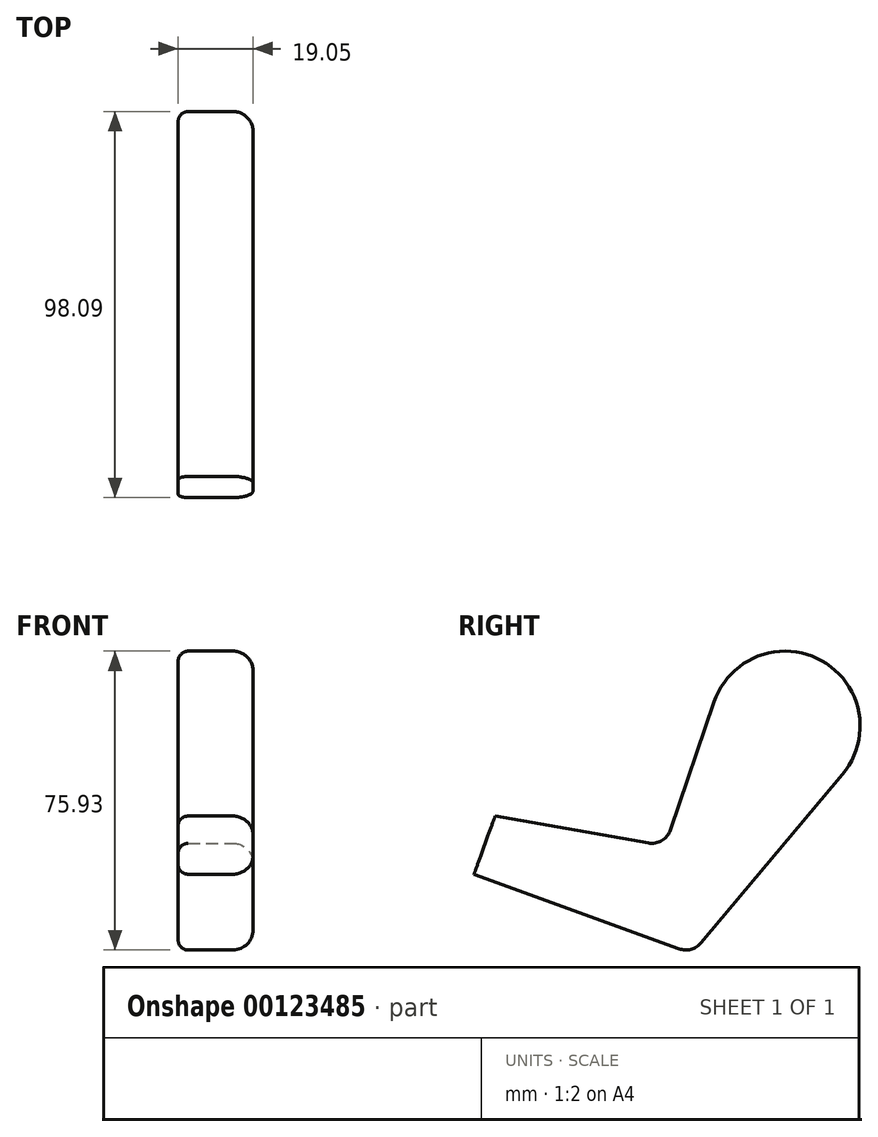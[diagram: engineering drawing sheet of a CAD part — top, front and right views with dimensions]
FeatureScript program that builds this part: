
annotation { "Feature Type Name" : "Feature", "Feature Type Description" : "" }
export const myFeature = defineFeature(function(context is Context, id is Id, definition is map)
    precondition{}
    {
        {
            var Q0;
            Q0=qCreatedBy(makeId("Front.planeOp"),FACE);
            var sketch = newSketch(context, id + "F0", { "sketchPlane" : qUnion([Q0])});
            skLineSegment(sketch, "E0", {"start": v(-26.99, 0) * mm, "end": v(26.99, 0) * mm});
            skLineSegment(sketch, "E1", {"start": v(26.99, 0) * mm, "end": v(38.1, 57.15) * mm});
            skLineSegment(sketch, "E2", {"start": v(38.1, 57.15) * mm, "end": v(38.1, 101.6) * mm});
            skLineSegment(sketch, "E3", {"start": v(38.1, 101.6) * mm, "end": v(-38.1, 101.6) * mm});
            skLineSegment(sketch, "E4", {"start": v(-38.1, 101.6) * mm, "end": v(-38.1, 57.15) * mm});
            skLineSegment(sketch, "E5", {"start": v(-38.1, 57.15) * mm, "end": v(-26.99, 0) * mm});
            skLineSegment(sketch, "E6", {"start": v(0, 0) * mm, "end": v(0, 101.6) * mm, "construction": true});
            skSolve(sketch);
        }
        {
            var Q0;
            Q0=qSketchRegion(id+"F0",true);
            extrude(context, id + "F1", {"entities" : qUnion([Q0]), "endBound" : BoundingType.SYMMETRIC, "depth" : 38.1 * mm});
        }
        {
            var Q0;
            Q0=makeQuery(id+"F1.opExtrude","CAP_EDGE",EDGE,{"disambiguationData":[OSD([sQuery(id+"F0.wireOp",EDGE,"E3")])],"isStart":false});
            var Q1;
            Q1=makeQuery(id+"F1.opExtrude","CAP_EDGE",EDGE,{"disambiguationData":[OSD([sQuery(id+"F0.wireOp",EDGE,"E3")])],"isStart":true});
            fillet(context, id + "F2", {"entities" : qUnion([Q0, Q1]), "radius" : 19.05 * mm, "tangentPropagation" : true, "allowEdgeOverflow" : false});
        }
        {
            var Q0;
            Q0=qCreatedBy(makeId("Front.planeOp"),FACE);
            var sketch = newSketch(context, id + "F3", { "sketchPlane" : qUnion([Q0])});
            skLineSegment(sketch, "E7.bottom", {"start": v(0, 82.55) * mm, "end": v(12.7, 82.55) * mm});
            skLineSegment(sketch, "E7.top", {"start": v(0, 120.65) * mm, "end": v(12.7, 120.65) * mm});
            skLineSegment(sketch, "E7.left", {"start": v(0, 82.55) * mm, "end": v(0, 120.65) * mm});
            skLineSegment(sketch, "E7.right", {"start": v(12.7, 82.55) * mm, "end": v(12.7, 120.65) * mm});
            skLineSegment(sketch, "E8", {"start": v(0, 82.55) * mm, "end": v(0, 0) * mm, "construction": true});
            skSolve(sketch);
        }
        {
            var Q0;
            Q0=qSketchRegion(id+"F3",true);
            var Q1;
            Q1=sQuery(id+"F3.wireOp",EDGE,"E8");
            revolve(context, id + "F4", {"operationType" : NewBodyOperationType.ADD, "entities" : qUnion([Q0]), "axis" : qUnion([Q1]), "revolveType" : RevolveType.FULL});
        }
        {
            var Q0;
            Q0=qCreatedBy(makeId("Right.planeOp"),FACE);
            var sketch = newSketch(context, id + "F5", { "sketchPlane" : qUnion([Q0])});
            skLineSegment(sketch, "E9", {"start": v(-5.08, 102.24) * mm, "end": v(-5.08, 158.12) * mm});
            skEllipticalArc(sketch, "E10", {});
            skLineSegment(sketch, "E11", {"start": v(-5.08, 102.24) * mm, "end": v(-5.08, 8.32) * mm, "construction": true});
            skLineSegment(sketch, "E12", {"start": v(-5.08, 130.18) * mm, "end": v(17.14, 130.18) * mm, "construction": true});
            const initialGuessF5  = {"E10": [-0.00508, 0.130175, 0, 1, 0.02794, 0.022225, 3.141592653589793, 0]};
            skSetInitialGuess(sketch, initialGuessF5);
            skSolve(sketch);
        }
        {
            var Q0;
            Q0=qSketchRegion(id+"F5",true);
            var Q1;
            Q1=sQuery(id+"F5.wireOp",EDGE,"E11");
            revolve(context, id + "F6", {"operationType" : NewBodyOperationType.ADD, "entities" : qUnion([Q0]), "axis" : qUnion([Q1]), "revolveType" : RevolveType.FULL});
        }
        {
            var Q0;
            Q0=makeQuery(id+"F1.opExtrude","SWEPT_EDGE",EDGE,{"disambiguationData":[OSD([sQuery(id+"F0.wireOp",EDGE,"E4"),sQuery(id+"F0.wireOp",EDGE,"E5")])]});
            var Q1;
            Q1=makeQuery(id+"F1.opExtrude","SWEPT_EDGE",EDGE,{"disambiguationData":[OSD([sQuery(id+"F0.wireOp",EDGE,"E1"),sQuery(id+"F0.wireOp",EDGE,"E2")])]});
            fillet(context, id + "F7", {"entities" : qUnion([Q0, Q1]), "radius" : 3.17 * mm, "tangentPropagation" : true, "allowEdgeOverflow" : false});
        }
        {
            var Q0;
            Q0=makeQuery(id+"F1.opExtrude","CAP_EDGE",EDGE,{"disambiguationData":[OSD([sQuery(id+"F0.wireOp",EDGE,"E1")])],"isStart":false});
            var Q1;
            Q1=makeQuery(id+"F1.opExtrude","CAP_EDGE",EDGE,{"disambiguationData":[OSD([sQuery(id+"F0.wireOp",EDGE,"E5")])],"isStart":false});
            fillet(context, id + "F8", {"entities" : qUnion([Q0, Q1]), "radius" : 3.17 * mm, "tangentPropagation" : true, "allowEdgeOverflow" : false});
        }
        {
            var Q0;
            Q0=makeQuery(id+"F1.opExtrude","SWEPT_FACE",FACE,{"disambiguationData":[OSD([sQuery(id+"F0.wireOp",EDGE,"E2")])]});
            var sketch = newSketch(context, id + "F9", { "sketchPlane" : qUnion([Q0])});
            skLineSegment(sketch, "E13", {"start": v(14.6, 70.3) * mm, "end": v(-23.62, 24.76) * mm});
            skLineSegment(sketch, "E14", {"start": v(-23.62, 24.76) * mm, "end": v(-79.04, 44.93) * mm});
            skLineSegment(sketch, "E15", {"start": v(-79.04, 44.93) * mm, "end": v(-73.66, 59.7) * mm});
            skLineSegment(sketch, "E16", {"start": v(-73.66, 59.7) * mm, "end": v(-30.48, 52.08) * mm});
            skLineSegment(sketch, "E17", {"start": v(-30.48, 52.08) * mm, "end": v(-18.04, 88.68) * mm});
            skArc(sketch, "E18.0", {"start": v(-18.04, 88.68) * mm, "mid": v(9.35, 99.15) * mm, "end": v(14.6, 70.3) * mm});
            skPoint(sketch, "E19.orphan", {"position": v(-19.05, 82.55) * mm});
            skPoint(sketch, "E20.orphan", {"position": v(19.05, 82.55) * mm});
            skSolve(sketch);
        }
        {
            var Q0;
            Q0=qSketchRegion(id+"F9",true);
            extrude(context, id + "F10", {"entities" : qUnion([Q0]), "depth" : 19.05 * mm});
        }
        {
            var Q0;
            Q0=makeQuery(id+"F10.opExtrude","SWEPT_EDGE",EDGE,{"disambiguationData":[OSD([sQuery(id+"F9.wireOp",EDGE,"E16"),sQuery(id+"F9.wireOp",EDGE,"E17")])]});
            var Q1;
            Q1=makeQuery(id+"FG809VM8ehI65F2_1.1.F10.opExtrude","SWEPT_EDGE",EDGE,{"disambiguationData":[OSD([sQuery(id+"F9.wireOp",EDGE,"E16"),sQuery(id+"F9.wireOp",EDGE,"E17")])]});
            fillet(context, id + "F11", {"entities" : qUnion([Q0, Q1]), "radius" : 5.08 * mm, "tangentPropagation" : true, "allowEdgeOverflow" : false});
        }
        {
            var Q0;
            Q0=makeQuery(id+"F10.opExtrude","SWEPT_EDGE",EDGE,{"disambiguationData":[OSD([sQuery(id+"F9.wireOp",EDGE,"E13"),sQuery(id+"F9.wireOp",EDGE,"E14")])]});
            var Q1;
            Q1=makeQuery(id+"FG809VM8ehI65F2_1.1.F10.opExtrude","SWEPT_EDGE",EDGE,{"disambiguationData":[OSD([sQuery(id+"F9.wireOp",EDGE,"E13"),sQuery(id+"F9.wireOp",EDGE,"E14")])]});
            fillet(context, id + "F12", {"entities" : qUnion([Q0, Q1]), "radius" : 5.08 * mm, "tangentPropagation" : true, "allowEdgeOverflow" : false});
        }
        {
            var Q0;
            Q0=makeQuery(id+"F10.opExtrude","CAP_EDGE",EDGE,{"disambiguationData":[OSD([sQuery(id+"F9.wireOp",EDGE,"E13")])],"isStart":false});
            var Q1;
            Q1=makeQuery(id+"FG809VM8ehI65F2_1.1.F10.opExtrude","CAP_EDGE",EDGE,{"disambiguationData":[OSD([sQuery(id+"F9.wireOp",EDGE,"E13")])],"isStart":false});
            fillet(context, id + "F13", {"entities" : qUnion([Q0, Q1]), "radius" : 5.08 * mm, "tangentPropagation" : true, "allowEdgeOverflow" : false});
        }
        {
            var Q0;
            Q0=makeQuery(id+"FG809VM8ehI65F2_1.1.F10.opExtrude","CAP_EDGE",EDGE,{"disambiguationData":[OSD([sQuery(id+"F9.wireOp",EDGE,"E14")])],"isStart":true});
            var Q1;
            Q1=makeQuery(id+"FG809VM8ehI65F2_1.1.F10.opExtrude","CAP_EDGE",EDGE,{"disambiguationData":[OSD([sQuery(id+"F9.wireOp",EDGE,"E16")])],"isStart":true});
            var Q2;
            {var subQ0=sQuery(id+"F9.wireOp",EDGE,"E17");var subQ1=sQuery(id+"F9.wireOp",EDGE,"E16");Q2=makeQuery(id+"F11.opFillet","BLEND_EDGE",EDGE,{"blendedFrom":[makeQuery(id+"FG809VM8ehI65F2_1.1.F10.opExtrude","SWEPT_EDGE",EDGE,{"disambiguationData":[OSD([subQ1,subQ0])]}),makeQuery(id+"FG809VM8ehI65F2_1.1.F10.opExtrude","CAP_FACE",FACE,{"disambiguationData":[OSD([sQuery(id+"F9.wireOp",EDGE,"E13"),sQuery(id+"F9.wireOp",EDGE,"E14"),sQuery(id+"F9.wireOp",EDGE,"E15"),subQ1,subQ0,sQuery(id+"F9.wireOp",EDGE,"E18.0")])],"isStart":true})],"blendedInto":[makeQuery(id+"FG809VM8ehI65F2_1.1.F10.opExtrude","CAP_FACE",FACE,{"disambiguationData":[OSD([sQuery(id+"F9.wireOp",EDGE,"E13"),sQuery(id+"F9.wireOp",EDGE,"E14"),sQuery(id+"F9.wireOp",EDGE,"E15"),subQ1,subQ0,sQuery(id+"F9.wireOp",EDGE,"E18.0")])],"isStart":true})]});}
            var Q3;
            Q3=makeQuery(id+"FG809VM8ehI65F2_1.1.F10.opExtrude","CAP_EDGE",EDGE,{"disambiguationData":[OSD([sQuery(id+"F9.wireOp",EDGE,"E17")])],"isStart":true});
            var Q4;
            {var subQ0=sQuery(id+"F9.wireOp",EDGE,"E17");var subQ2=sQuery(id+"F9.wireOp",EDGE,"E18.0");Q4=makeQuery(id+"FG809VM8ehI65F2_1.1.F10.boolean.opBoolean","SPLIT",EDGE,{"disambiguationData":[TD([makeQuery(id+"FG809VM8ehI65F2_1.1.F10.opExtrude","SWEPT_FACE",FACE,{"disambiguationData":[OSD([subQ0])]})])],"derivedFrom":makeQuery(id+"FG809VM8ehI65F2_1.1.F10.opExtrude","CAP_EDGE",EDGE,{"disambiguationData":[OSD([subQ2])],"isStart":true})});}
            var Q5;
            {var subQ0=sQuery(id+"F9.wireOp",EDGE,"E13");var subQ1=sQuery(id+"F9.wireOp",EDGE,"E14");Q5=makeQuery(id+"FG809VM8ehI65F2_1.1.F10.boolean.opBoolean","SPLIT",EDGE,{"disambiguationData":[TD([makeQuery(id+"FG809VM8ehI65F2_1.1.F10.opExtrude","SWEPT_FACE",FACE,{"disambiguationData":[OSD([subQ1])]})])],"derivedFrom":makeQuery(id+"FG809VM8ehI65F2_1.1.F10.opExtrude","CAP_EDGE",EDGE,{"disambiguationData":[OSD([subQ0])],"isStart":true})});}
            var Q6;
            {var subQ0=sQuery(id+"F9.wireOp",EDGE,"E14");var subQ1=sQuery(id+"F9.wireOp",EDGE,"E13");Q6=makeQuery(id+"F12.opFillet","BLEND_EDGE",EDGE,{"blendedFrom":[makeQuery(id+"FG809VM8ehI65F2_1.1.F10.opExtrude","SWEPT_EDGE",EDGE,{"disambiguationData":[OSD([subQ1,subQ0])]}),makeQuery(id+"FG809VM8ehI65F2_1.1.F10.opExtrude","CAP_FACE",FACE,{"disambiguationData":[OSD([subQ1,subQ0,sQuery(id+"F9.wireOp",EDGE,"E15"),sQuery(id+"F9.wireOp",EDGE,"E16"),sQuery(id+"F9.wireOp",EDGE,"E17"),sQuery(id+"F9.wireOp",EDGE,"E18.0")])],"isStart":true})],"blendedInto":[makeQuery(id+"FG809VM8ehI65F2_1.1.F10.opExtrude","CAP_FACE",FACE,{"disambiguationData":[OSD([subQ1,subQ0,sQuery(id+"F9.wireOp",EDGE,"E15"),sQuery(id+"F9.wireOp",EDGE,"E16"),sQuery(id+"F9.wireOp",EDGE,"E17"),sQuery(id+"F9.wireOp",EDGE,"E18.0")])],"isStart":true})]});}
            var Q7;
            Q7=makeQuery(id+"F10.opExtrude","CAP_EDGE",EDGE,{"disambiguationData":[OSD([sQuery(id+"F9.wireOp",EDGE,"E13")])],"isStart":true});
            fillet(context, id + "F14", {"entities" : qUnion([Q0, Q1, Q2, Q3, Q4, Q5, Q6, Q7]), "radius" : 2.54 * mm, "tangentPropagation" : true, "allowEdgeOverflow" : false});
        }
        {
            var Q0;
            Q0=qCreatedBy(makeId("Front.planeOp"),FACE);
            var sketch = newSketch(context, id + "F15", { "sketchPlane" : qUnion([Q0])});
            skLineSegment(sketch, "E21.bottom", {"start": v(-38.1, 162.47) * mm, "end": v(38.1, 162.47) * mm});
            skLineSegment(sketch, "E21.top", {"start": v(-38.1, 0) * mm, "end": v(38.1, 0) * mm});
            skLineSegment(sketch, "E21.left", {"start": v(-38.1, 162.47) * mm, "end": v(-38.1, 0) * mm});
            skLineSegment(sketch, "E21.right", {"start": v(38.1, 162.47) * mm, "end": v(38.1, 0) * mm});
            skSolve(sketch);
        }
        {
            var Q0;
            Q0=qSketchRegion(id+"F15",true);
            extrude(context, id + "F16", {"entities" : qUnion([Q0]), "operationType" : NewBodyOperationType.REMOVE, "endBound" : BoundingType.SYMMETRIC, "depth" : 63.5 * mm});
        }
    });
